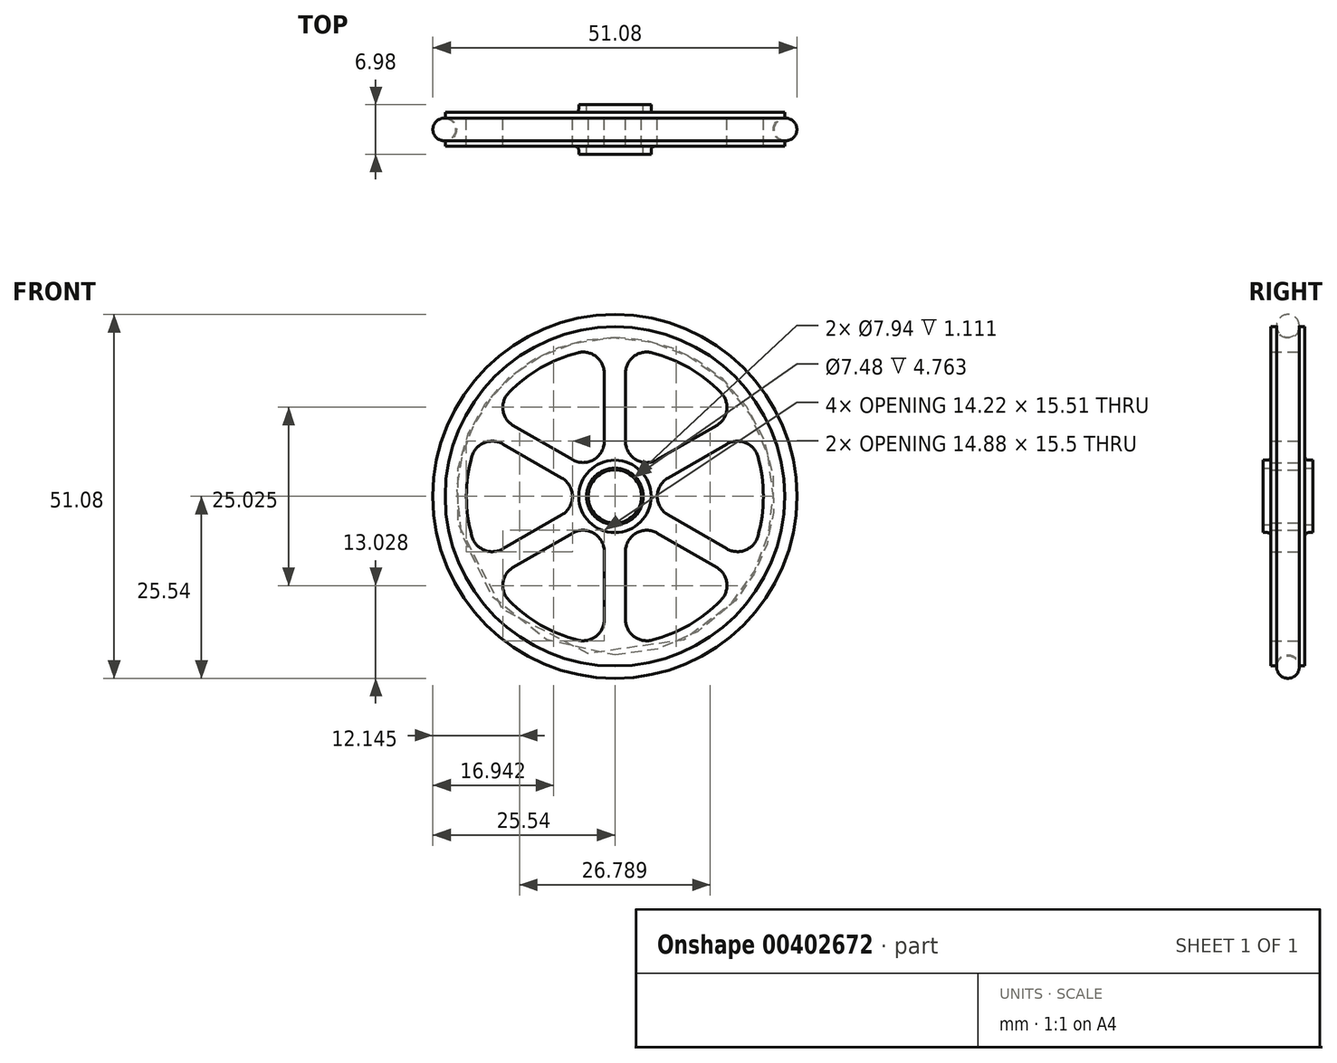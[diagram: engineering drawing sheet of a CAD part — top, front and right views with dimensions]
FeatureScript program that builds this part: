
annotation { "Feature Type Name" : "Feature", "Feature Type Description" : "" }
export const myFeature = defineFeature(function(context is Context, id is Id, definition is map)
    precondition{}
    {
        {
            var Q0;
            Q0=qCreatedBy(makeId("Front.planeOp"),FACE);
            var sketch = newSketch(context, id + "F0", { "sketchPlane" : qUnion([Q0])});
            skCircle(sketch, "E0", {"center": v(0, 0) * mm, "radius": 23.81 * mm});
            skArc(sketch, "E1.0", {"start": v(-5.2, 20.17) * mm, "mid": v(-10.42, 18.04) * mm, "end": v(-14.87, 14.6) * mm});
            skLineSegment(sketch, "E2", {"start": v(-2.98, 5.16) * mm, "end": v(-2.98, 5.16) * mm});
            skLineSegment(sketch, "E3.0", {"start": v(1.49, 23.81) * mm, "end": v(1.49, 23.77) * mm});
            skLineSegment(sketch, "E4.0", {"start": v(-1.49, 23.81) * mm, "end": v(-1.49, 23.77) * mm});
            skLineSegment(sketch, "E5.trimOffspring", {"start": v(-1.49, 17.3) * mm, "end": v(-1.49, 7.73) * mm});
            skLineSegment(sketch, "E6.trimOffspring", {"start": v(1.49, 17.3) * mm, "end": v(1.49, 7.73) * mm});
            skLineSegment(sketch, "E7.1.0", {"start": v(-14.23, 9.94) * mm, "end": v(-5.95, 5.16) * mm});
            skLineSegment(sketch, "E7.2.0", {"start": v(-15.72, -7.36) * mm, "end": v(-7.44, -2.58) * mm});
            skLineSegment(sketch, "E8.2.3.0", {"start": v(-1.49, -17.3) * mm, "end": v(-1.49, -7.73) * mm});
            skLineSegment(sketch, "E8.2.4.0", {"start": v(14.23, -9.94) * mm, "end": v(5.95, -5.16) * mm});
            skLineSegment(sketch, "E8.2.5.0", {"start": v(15.72, 7.36) * mm, "end": v(7.44, 2.58) * mm});
            skLineSegment(sketch, "E9.1.0", {"start": v(-15.72, 7.36) * mm, "end": v(-7.44, 2.58) * mm});
            skLineSegment(sketch, "E9.2.0", {"start": v(-14.23, -9.94) * mm, "end": v(-5.95, -5.16) * mm});
            skLineSegment(sketch, "E9.3.0", {"start": v(1.49, -17.3) * mm, "end": v(1.49, -7.73) * mm});
            skLineSegment(sketch, "E9.4.0", {"start": v(15.72, -7.36) * mm, "end": v(7.44, -2.58) * mm});
            skLineSegment(sketch, "E9.5.0", {"start": v(14.23, 9.94) * mm, "end": v(5.95, 5.16) * mm});
            skPoint(sketch, "E10.start.orphan", {"position": v(0, 23.81) * mm});
            skLineSegment(sketch, "E11.trimOffspring", {"start": v(2.98, 5.16) * mm, "end": v(2.98, 5.16) * mm});
            skArc(sketch, "E12.trimOffspring", {"start": v(14.87, 14.6) * mm, "mid": v(10.42, 18.04) * mm, "end": v(5.2, 20.17) * mm});
            skArc(sketch, "E13.trimOffspring", {"start": v(20.08, -5.58) * mm, "mid": v(20.84, 0) * mm, "end": v(20.08, 5.58) * mm});
            skArc(sketch, "E14.trimOffspring", {"start": v(5.2, -20.17) * mm, "mid": v(10.42, -18.04) * mm, "end": v(14.87, -14.6) * mm});
            skArc(sketch, "E15.trimOffspring", {"start": v(-14.87, -14.6) * mm, "mid": v(-10.42, -18.04) * mm, "end": v(-5.2, -20.17) * mm});
            skArc(sketch, "E16.trimOffspring", {"start": v(-20.08, 5.58) * mm, "mid": v(-20.84, 0) * mm, "end": v(-20.08, -5.58) * mm});
            skLineSegment(sketch, "E17.trimOffspring", {"start": v(-5.95, 0) * mm, "end": v(-5.95, 0) * mm});
            skLineSegment(sketch, "E18.trimOffspring", {"start": v(-2.98, -5.16) * mm, "end": v(-2.98, -5.16) * mm});
            skLineSegment(sketch, "E19.trimOffspring", {"start": v(2.98, -5.16) * mm, "end": v(2.98, -5.16) * mm});
            skLineSegment(sketch, "E20.trimOffspring", {"start": v(5.95, 0) * mm, "end": v(5.95, 0) * mm});
            skPoint(sketch, "E21.visualSharp", {"position": v(-1.49, 20.78) * mm});
            skArc(sketch, "E21.filletArc", {"start": v(-1.49, 17.3) * mm, "mid": v(-2.64, 19.65) * mm, "end": v(-5.2, 20.17) * mm});
            skPoint(sketch, "E22.visualSharp", {"position": v(-1.49, 5.76) * mm});
            skArc(sketch, "E22.filletArc", {"start": v(-2.98, 5.16) * mm, "mid": v(-1.89, 6.25) * mm, "end": v(-1.49, 7.73) * mm});
            skPoint(sketch, "E23.visualSharp", {"position": v(-4.25, 4.17) * mm});
            skArc(sketch, "E23.filletArc", {"start": v(-5.95, 5.16) * mm, "mid": v(-4.46, 4.76) * mm, "end": v(-2.98, 5.16) * mm});
            skPoint(sketch, "E24.visualSharp", {"position": v(-17.25, 11.68) * mm});
            skArc(sketch, "E24.filletArc", {"start": v(-14.87, 14.6) * mm, "mid": v(-15.7, 12.11) * mm, "end": v(-14.23, 9.94) * mm});
            skPoint(sketch, "E25.visualSharp", {"position": v(-18.74, 9.1) * mm});
            skArc(sketch, "E25.filletArc", {"start": v(-15.72, 7.36) * mm, "mid": v(-18.33, 7.53) * mm, "end": v(-20.08, 5.58) * mm});
            skPoint(sketch, "E26.visualSharp", {"position": v(-5.74, 1.6) * mm});
            skArc(sketch, "E26.filletArc", {"start": v(-5.95, 0) * mm, "mid": v(-6.35, 1.49) * mm, "end": v(-7.44, 2.58) * mm});
            skPoint(sketch, "E27.visualSharp", {"position": v(-5.74, -1.6) * mm});
            skArc(sketch, "E27.filletArc", {"start": v(-7.44, -2.58) * mm, "mid": v(-6.35, -1.49) * mm, "end": v(-5.95, 0) * mm});
            skPoint(sketch, "E28.visualSharp", {"position": v(-18.74, -9.1) * mm});
            skArc(sketch, "E28.filletArc", {"start": v(-20.08, -5.58) * mm, "mid": v(-18.33, -7.53) * mm, "end": v(-15.72, -7.36) * mm});
            skPoint(sketch, "E29.visualSharp", {"position": v(-17.25, -11.68) * mm});
            skArc(sketch, "E29.filletArc", {"start": v(-14.23, -9.94) * mm, "mid": v(-15.7, -12.11) * mm, "end": v(-14.87, -14.6) * mm});
            skPoint(sketch, "E30.visualSharp", {"position": v(-1.49, -20.78) * mm});
            skArc(sketch, "E30.filletArc", {"start": v(-5.2, -20.17) * mm, "mid": v(-2.64, -19.65) * mm, "end": v(-1.49, -17.3) * mm});
            skPoint(sketch, "E31.visualSharp", {"position": v(1.49, -20.78) * mm});
            skArc(sketch, "E31.filletArc", {"start": v(1.49, -17.3) * mm, "mid": v(2.64, -19.65) * mm, "end": v(5.2, -20.17) * mm});
            skPoint(sketch, "E32.visualSharp", {"position": v(17.25, -11.68) * mm});
            skArc(sketch, "E32.filletArc", {"start": v(14.87, -14.6) * mm, "mid": v(15.7, -12.11) * mm, "end": v(14.23, -9.94) * mm});
            skPoint(sketch, "E33.visualSharp", {"position": v(4.25, -4.17) * mm});
            skArc(sketch, "E33.filletArc", {"start": v(5.95, -5.16) * mm, "mid": v(4.46, -4.76) * mm, "end": v(2.98, -5.16) * mm});
            skPoint(sketch, "E34.visualSharp", {"position": v(1.49, -5.76) * mm});
            skArc(sketch, "E34.filletArc", {"start": v(2.98, -5.16) * mm, "mid": v(1.89, -6.25) * mm, "end": v(1.49, -7.73) * mm});
            skPoint(sketch, "E35.visualSharp", {"position": v(-1.49, -5.76) * mm});
            skArc(sketch, "E35.filletArc", {"start": v(-1.49, -7.73) * mm, "mid": v(-1.89, -6.25) * mm, "end": v(-2.98, -5.16) * mm});
            skPoint(sketch, "E36.visualSharp", {"position": v(-4.25, -4.17) * mm});
            skArc(sketch, "E36.filletArc", {"start": v(-2.98, -5.16) * mm, "mid": v(-4.46, -4.76) * mm, "end": v(-5.95, -5.16) * mm});
            skPoint(sketch, "E37.visualSharp", {"position": v(5.74, -1.6) * mm});
            skArc(sketch, "E37.filletArc", {"start": v(5.95, 0) * mm, "mid": v(6.35, -1.49) * mm, "end": v(7.44, -2.58) * mm});
            skPoint(sketch, "E38.visualSharp", {"position": v(5.74, 1.6) * mm});
            skArc(sketch, "E38.filletArc", {"start": v(7.44, 2.58) * mm, "mid": v(6.35, 1.49) * mm, "end": v(5.95, 0) * mm});
            skPoint(sketch, "E39.visualSharp", {"position": v(4.25, 4.17) * mm});
            skArc(sketch, "E39.filletArc", {"start": v(2.98, 5.16) * mm, "mid": v(4.46, 4.76) * mm, "end": v(5.95, 5.16) * mm});
            skPoint(sketch, "E40.visualSharp", {"position": v(1.49, 5.76) * mm});
            skArc(sketch, "E40.filletArc", {"start": v(1.49, 7.73) * mm, "mid": v(1.89, 6.25) * mm, "end": v(2.98, 5.16) * mm});
            skPoint(sketch, "E41.visualSharp", {"position": v(1.49, 20.78) * mm});
            skArc(sketch, "E41.filletArc", {"start": v(5.2, 20.17) * mm, "mid": v(2.64, 19.65) * mm, "end": v(1.49, 17.3) * mm});
            skPoint(sketch, "E42.visualSharp", {"position": v(17.25, 11.68) * mm});
            skArc(sketch, "E42.filletArc", {"start": v(14.23, 9.94) * mm, "mid": v(15.7, 12.11) * mm, "end": v(14.87, 14.6) * mm});
            skPoint(sketch, "E43.visualSharp", {"position": v(18.74, 9.1) * mm});
            skArc(sketch, "E43.filletArc", {"start": v(20.08, 5.58) * mm, "mid": v(18.33, 7.53) * mm, "end": v(15.72, 7.36) * mm});
            skPoint(sketch, "E44.visualSharp", {"position": v(18.74, -9.1) * mm});
            skArc(sketch, "E44.filletArc", {"start": v(15.72, -7.36) * mm, "mid": v(18.33, -7.53) * mm, "end": v(20.08, -5.58) * mm});
            skCircle(sketch, "E45", {"center": v(0, 0) * mm, "radius": 3.74 * mm});
            skSolve(sketch);
        }
        {
            var Q0;
            Q0 = qSketchRegion(id + "F0", true);
            extrude(context, id + "F1", {"entities" : qUnion([Q0]), "endBound" : BoundingType.SYMMETRIC, "depth" : 4.76 * mm});
        }
        {
            var Q0;
            Q0=qCreatedBy(makeId("Right.planeOp"),FACE);
            var sketch = newSketch(context, id + "F2", { "sketchPlane" : qUnion([Q0])});
            skCircle(sketch, "E46", {"center": v(0, 23.81) * mm, "radius": 1.59 * mm});
            skLineSegment(sketch, "E47", {"start": v(11.99, 0) * mm, "end": v(-10.98, 0) * mm, "construction": true});
            skSolve(sketch);
        }
        {
            var Q0;
            Q0 = qSketchRegion(id + "F2", true);
            var Q1;
            Q1=sQuery(id+"F2.wireOp",EDGE,"E47");
            revolve(context, id + "F3", {"operationType" : NewBodyOperationType.REMOVE, "entities" : qUnion([Q0]), "axis" : qUnion([Q1]), "revolveType" : RevolveType.FULL, "oppositeDirection" : true});
        }
        {
            var Q0;
            Q0=qCreatedBy(makeId("Front.planeOp"),FACE);
            var sketch = newSketch(context, id + "F4", { "sketchPlane" : qUnion([Q0])});
            skCircle(sketch, "E48", {"center": v(0, 0) * mm, "radius": 5.08 * mm});
            skCircle(sketch, "E49", {"center": v(0, 0) * mm, "radius": 3.97 * mm});
            skSolve(sketch);
        }
        {
            var Q0;
            Q0 = qSketchRegion(id + "F4", true);
            extrude(context, id + "F5", {"entities" : qUnion([Q0]), "operationType" : NewBodyOperationType.ADD, "endBound" : BoundingType.SYMMETRIC, "depth" : 7 * mm});
        }
        {
            var Q0;
            Q0=makeQuery(id+"F5.boolean.opBoolean","INTERSECT",EDGE,{"derivedFrom":[makeQuery(id+"F1.opExtrude","CAP_FACE",FACE,{"disambiguationData":[OSD([sQuery(id+"F0.wireOp",EDGE,"E0"),sQuery(id+"F0.wireOp",EDGE,"E1.0"),sQuery(id+"F0.wireOp",EDGE,"VTbdK5Mh-5Ee1-NDTS-Pil0-HizmJrwj2FMA"),sQuery(id+"F0.wireOp",EDGE,"E5.trimOffspring"),sQuery(id+"F0.wireOp",EDGE,"E6.trimOffspring"),sQuery(id+"F0.wireOp",EDGE,"E7.1.0"),sQuery(id+"F0.wireOp",EDGE,"E7.2.0"),sQuery(id+"F0.wireOp",EDGE,"E8.2.3.0"),sQuery(id+"F0.wireOp",EDGE,"E8.2.4.0"),sQuery(id+"F0.wireOp",EDGE,"E8.2.5.0"),sQuery(id+"F0.wireOp",EDGE,"E9.1.0"),sQuery(id+"F0.wireOp",EDGE,"E9.2.0"),sQuery(id+"F0.wireOp",EDGE,"E9.3.0"),sQuery(id+"F0.wireOp",EDGE,"E9.4.0"),sQuery(id+"F0.wireOp",EDGE,"E9.5.0"),sQuery(id+"F0.wireOp",EDGE,"E12.trimOffspring"),sQuery(id+"F0.wireOp",EDGE,"E13.trimOffspring"),sQuery(id+"F0.wireOp",EDGE,"E14.trimOffspring"),sQuery(id+"F0.wireOp",EDGE,"E15.trimOffspring"),sQuery(id+"F0.wireOp",EDGE,"E16.trimOffspring"),sQuery(id+"F0.wireOp",EDGE,"E21.filletArc"),sQuery(id+"F0.wireOp",EDGE,"E22.filletArc"),sQuery(id+"F0.wireOp",EDGE,"E23.filletArc"),sQuery(id+"F0.wireOp",EDGE,"E24.filletArc"),sQuery(id+"F0.wireOp",EDGE,"E25.filletArc"),sQuery(id+"F0.wireOp",EDGE,"E26.filletArc"),sQuery(id+"F0.wireOp",EDGE,"E27.filletArc"),sQuery(id+"F0.wireOp",EDGE,"E28.filletArc"),sQuery(id+"F0.wireOp",EDGE,"E29.filletArc"),sQuery(id+"F0.wireOp",EDGE,"E30.filletArc"),sQuery(id+"F0.wireOp",EDGE,"E31.filletArc"),sQuery(id+"F0.wireOp",EDGE,"E32.filletArc"),sQuery(id+"F0.wireOp",EDGE,"E33.filletArc"),sQuery(id+"F0.wireOp",EDGE,"E34.filletArc"),sQuery(id+"F0.wireOp",EDGE,"E35.filletArc"),sQuery(id+"F0.wireOp",EDGE,"E36.filletArc"),sQuery(id+"F0.wireOp",EDGE,"E37.filletArc"),sQuery(id+"F0.wireOp",EDGE,"E38.filletArc"),sQuery(id+"F0.wireOp",EDGE,"E39.filletArc"),sQuery(id+"F0.wireOp",EDGE,"E40.filletArc"),sQuery(id+"F0.wireOp",EDGE,"E41.filletArc"),sQuery(id+"F0.wireOp",EDGE,"E42.filletArc"),sQuery(id+"F0.wireOp",EDGE,"E43.filletArc"),sQuery(id+"F0.wireOp",EDGE,"E44.filletArc")])],"isStart":false}),makeQuery(id+"F5.opExtrude","SWEPT_FACE",FACE,{"disambiguationData":[OSD([sQuery(id+"F4.wireOp",EDGE,"E48")])]})]});
            var Q1;
            Q1=makeQuery(id+"F5.boolean.opBoolean","INTERSECT",EDGE,{"derivedFrom":[makeQuery(id+"F1.opExtrude","CAP_FACE",FACE,{"disambiguationData":[OSD([sQuery(id+"F0.wireOp",EDGE,"E0"),sQuery(id+"F0.wireOp",EDGE,"E1.0"),sQuery(id+"F0.wireOp",EDGE,"VTbdK5Mh-5Ee1-NDTS-Pil0-HizmJrwj2FMA"),sQuery(id+"F0.wireOp",EDGE,"E5.trimOffspring"),sQuery(id+"F0.wireOp",EDGE,"E6.trimOffspring"),sQuery(id+"F0.wireOp",EDGE,"E7.1.0"),sQuery(id+"F0.wireOp",EDGE,"E7.2.0"),sQuery(id+"F0.wireOp",EDGE,"E8.2.3.0"),sQuery(id+"F0.wireOp",EDGE,"E8.2.4.0"),sQuery(id+"F0.wireOp",EDGE,"E8.2.5.0"),sQuery(id+"F0.wireOp",EDGE,"E9.1.0"),sQuery(id+"F0.wireOp",EDGE,"E9.2.0"),sQuery(id+"F0.wireOp",EDGE,"E9.3.0"),sQuery(id+"F0.wireOp",EDGE,"E9.4.0"),sQuery(id+"F0.wireOp",EDGE,"E9.5.0"),sQuery(id+"F0.wireOp",EDGE,"E12.trimOffspring"),sQuery(id+"F0.wireOp",EDGE,"E13.trimOffspring"),sQuery(id+"F0.wireOp",EDGE,"E14.trimOffspring"),sQuery(id+"F0.wireOp",EDGE,"E15.trimOffspring"),sQuery(id+"F0.wireOp",EDGE,"E16.trimOffspring"),sQuery(id+"F0.wireOp",EDGE,"E21.filletArc"),sQuery(id+"F0.wireOp",EDGE,"E22.filletArc"),sQuery(id+"F0.wireOp",EDGE,"E23.filletArc"),sQuery(id+"F0.wireOp",EDGE,"E24.filletArc"),sQuery(id+"F0.wireOp",EDGE,"E25.filletArc"),sQuery(id+"F0.wireOp",EDGE,"E26.filletArc"),sQuery(id+"F0.wireOp",EDGE,"E27.filletArc"),sQuery(id+"F0.wireOp",EDGE,"E28.filletArc"),sQuery(id+"F0.wireOp",EDGE,"E29.filletArc"),sQuery(id+"F0.wireOp",EDGE,"E30.filletArc"),sQuery(id+"F0.wireOp",EDGE,"E31.filletArc"),sQuery(id+"F0.wireOp",EDGE,"E32.filletArc"),sQuery(id+"F0.wireOp",EDGE,"E33.filletArc"),sQuery(id+"F0.wireOp",EDGE,"E34.filletArc"),sQuery(id+"F0.wireOp",EDGE,"E35.filletArc"),sQuery(id+"F0.wireOp",EDGE,"E36.filletArc"),sQuery(id+"F0.wireOp",EDGE,"E37.filletArc"),sQuery(id+"F0.wireOp",EDGE,"E38.filletArc"),sQuery(id+"F0.wireOp",EDGE,"E39.filletArc"),sQuery(id+"F0.wireOp",EDGE,"E40.filletArc"),sQuery(id+"F0.wireOp",EDGE,"E41.filletArc"),sQuery(id+"F0.wireOp",EDGE,"E42.filletArc"),sQuery(id+"F0.wireOp",EDGE,"E43.filletArc"),sQuery(id+"F0.wireOp",EDGE,"E44.filletArc")])],"isStart":true}),makeQuery(id+"F5.opExtrude","SWEPT_FACE",FACE,{"disambiguationData":[OSD([sQuery(id+"F4.wireOp",EDGE,"E48")])]})]});
            fillet(context, id + "F6", {"entities" : qUnion([Q0, Q1]), "radius" : 0.5 * mm, "tangentPropagation" : true, "allowEdgeOverflow" : false});
        }
        {
            var Q0;
            Q0=qCreatedBy(makeId("Right.planeOp"),FACE);
            var sketch = newSketch(context, id + "F7", { "sketchPlane" : qUnion([Q0])});
            skCircle(sketch, "E50", {"center": v(0, 23.95) * mm, "radius": 1.59 * mm});
            skLineSegment(sketch, "E51", {"start": v(15.25, 0) * mm, "end": v(-15.83, 0) * mm, "construction": true});
            skSolve(sketch);
        }
        {
            var Q0;
            Q0=makeQuery(id+"F7.imprint","IMPRINT",FACE,{"disambiguationData":[TD([[makeQuery(id+"F7.imprint","IMPRINT",EDGE,{"derivedFrom":sQuery(id+"F7.wireOp",EDGE,"E50")}),1.0]])]});
            var Q1;
            Q1=sQuery(id+"F7.wireOp",EDGE,"E51");
            revolve(context, id + "F8", {"operationType" : NewBodyOperationType.ADD, "entities" : qUnion([Q0]), "axis" : qUnion([Q1]), "revolveType" : RevolveType.FULL});
        }
    });
